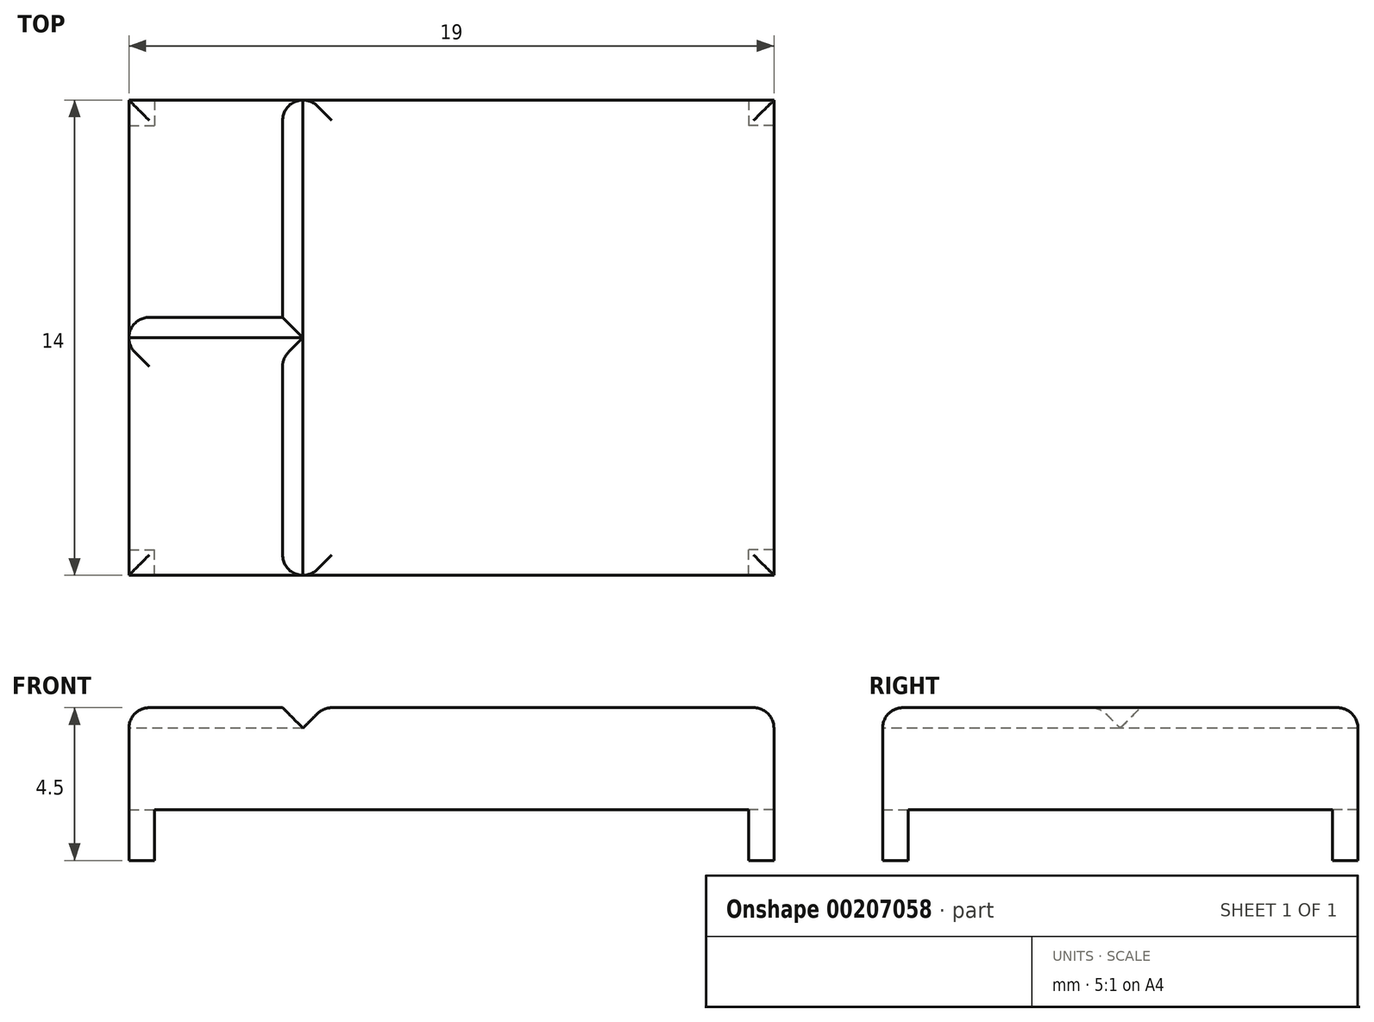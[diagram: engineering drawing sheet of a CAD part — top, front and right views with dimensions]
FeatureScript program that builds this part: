
annotation { "Feature Type Name" : "Feature", "Feature Type Description" : "" }
export const myFeature = defineFeature(function(context is Context, id is Id, definition is map)
    precondition{}
    {
        {
            var Q0;
            Q0=qCreatedBy(makeId("Top.planeOp"),FACE);
            var sketch = newSketch(context, id + "F0", { "sketchPlane" : qUnion([Q0])});
            skLineSegment(sketch, "E0.bottom", {"start": v(9.5, -7) * mm, "end": v(-9.5, -7) * mm});
            skLineSegment(sketch, "E0.top", {"start": v(9.5, 7) * mm, "end": v(-9.5, 7) * mm});
            skLineSegment(sketch, "E0.left", {"start": v(9.5, -7) * mm, "end": v(9.5, 7) * mm});
            skLineSegment(sketch, "E0.right", {"start": v(-9.5, -7) * mm, "end": v(-9.5, 7) * mm});
            skPoint(sketch, "E0.middle", {"position": v(0, 0) * mm});
            skSolve(sketch);
        }
        {
            var Q0;
            Q0=makeQuery(id+"F0.imprint","IMPRINT",FACE,{"disambiguationData":[TD([[makeQuery(id+"F0.imprint","IMPRINT",EDGE,{"derivedFrom":sQuery(id+"F0.wireOp",EDGE,"E0.bottom")}),-1.0]])]});
            extrude(context, id + "F1", {"entities" : qUnion([Q0]), "depth" : 3 * mm});
        }
        {
            var Q0;
            Q0=makeQuery(id+"F1.opExtrude","CAP_FACE",FACE,{"disambiguationData":[OSD([sQuery(id+"F0.wireOp",EDGE,"E0.bottom"),sQuery(id+"F0.wireOp",EDGE,"E0.top"),sQuery(id+"F0.wireOp",EDGE,"E0.left"),sQuery(id+"F0.wireOp",EDGE,"E0.right")])],"isStart":true});
            var sketch = newSketch(context, id + "F2", { "sketchPlane" : qUnion([Q0])});
            skLineSegment(sketch, "E1.bottom", {"start": v(9.5, 7) * mm, "end": v(8.75, 7) * mm});
            skLineSegment(sketch, "E1.top", {"start": v(9.5, 6.25) * mm, "end": v(8.75, 6.25) * mm});
            skLineSegment(sketch, "E1.left", {"start": v(9.5, 7) * mm, "end": v(9.5, 6.25) * mm});
            skLineSegment(sketch, "E1.right", {"start": v(8.75, 7) * mm, "end": v(8.75, 6.25) * mm});
            skLineSegment(sketch, "E2.bottom", {"start": v(-9.5, 7) * mm, "end": v(-8.75, 7) * mm});
            skLineSegment(sketch, "E2.top", {"start": v(-9.5, 6.25) * mm, "end": v(-8.75, 6.25) * mm});
            skLineSegment(sketch, "E2.left", {"start": v(-9.5, 7) * mm, "end": v(-9.5, 6.25) * mm});
            skLineSegment(sketch, "E2.right", {"start": v(-8.75, 7) * mm, "end": v(-8.75, 6.25) * mm});
            skLineSegment(sketch, "E3.bottom", {"start": v(-9.5, -7) * mm, "end": v(-8.75, -7) * mm});
            skLineSegment(sketch, "E3.top", {"start": v(-9.5, -6.25) * mm, "end": v(-8.75, -6.25) * mm});
            skLineSegment(sketch, "E3.left", {"start": v(-9.5, -7) * mm, "end": v(-9.5, -6.25) * mm});
            skLineSegment(sketch, "E3.right", {"start": v(-8.75, -7) * mm, "end": v(-8.75, -6.25) * mm});
            skLineSegment(sketch, "E4.bottom", {"start": v(9.5, -7) * mm, "end": v(8.75, -7) * mm});
            skLineSegment(sketch, "E4.top", {"start": v(9.5, -6.25) * mm, "end": v(8.75, -6.25) * mm});
            skLineSegment(sketch, "E4.left", {"start": v(9.5, -7) * mm, "end": v(9.5, -6.25) * mm});
            skLineSegment(sketch, "E4.right", {"start": v(8.75, -7) * mm, "end": v(8.75, -6.25) * mm});
            skSolve(sketch);
        }
        {
            var Q0;
            Q0=qSketchRegion(id+"F2",true);
            extrude(context, id + "F3", {"entities" : qUnion([Q0]), "operationType" : NewBodyOperationType.ADD, "depth" : 1.5 * mm});
        }
        {
            var Q0;
            Q0=makeQuery(id+"F3.boolean.opBoolean","MERGE",FACE,{"derivedFrom":[makeQuery(id+"F1.opExtrude","SWEPT_FACE",FACE,{"disambiguationData":[OSD([sQuery(id+"F0.wireOp",EDGE,"E0.bottom")])]}),makeQuery(id+"F3.opExtrude","SWEPT_FACE",FACE,{"disambiguationData":[OSD([sQuery(id+"F2.wireOp",EDGE,"E1.bottom")])]}),makeQuery(id+"F3.opExtrude","SWEPT_FACE",FACE,{"disambiguationData":[OSD([sQuery(id+"F2.wireOp",EDGE,"E2.bottom")])]})]});
            var sketch = newSketch(context, id + "F4", { "sketchPlane" : qUnion([Q0])});
            skLineSegment(sketch, "E5", {"start": v(-4.97, 3) * mm, "end": v(-4.37, 2.4) * mm});
            skLineSegment(sketch, "E6", {"start": v(-4.37, 2.4) * mm, "end": v(-3.77, 3) * mm});
            skSolve(sketch);
        }
        {
            var Q0;
            {var subQ0=sQuery(id+"F4.wireOp",EDGE,"E5");Q0=makeQuery(id+"F4.imprint","IMPRINT",FACE,{"disambiguationData":[TD([[makeQuery(id+"F4.imprint","IMPRINT",EDGE,{"derivedFrom":subQ0}),1.0]])]});}
            extrude(context, id + "F5", {"entities" : qUnion([Q0]), "operationType" : NewBodyOperationType.REMOVE, "endBound" : BoundingType.THROUGH_ALL, "oppositeDirection" : true, "depth" : 25 * mm});
        }
        {
            var Q0;
            Q0=makeQuery(id+"F3.boolean.opBoolean","MERGE",FACE,{"derivedFrom":[makeQuery(id+"F1.opExtrude","SWEPT_FACE",FACE,{"disambiguationData":[OSD([sQuery(id+"F0.wireOp",EDGE,"E0.right")])]}),makeQuery(id+"F3.opExtrude","SWEPT_FACE",FACE,{"disambiguationData":[OSD([sQuery(id+"F2.wireOp",EDGE,"E2.left")])]}),makeQuery(id+"F3.opExtrude","SWEPT_FACE",FACE,{"disambiguationData":[OSD([sQuery(id+"F2.wireOp",EDGE,"E3.left")])]})]});
            var sketch = newSketch(context, id + "F6", { "sketchPlane" : qUnion([Q0])});
            skLineSegment(sketch, "E7", {"start": v(-0.6, 3) * mm, "end": v(0, 2.4) * mm});
            skPoint(sketch, "E7.endSnap0", {"position": v(0, 3) * mm});
            skLineSegment(sketch, "E8", {"start": v(0, 2.4) * mm, "end": v(0.6, 3) * mm});
            skSolve(sketch);
        }
        {
            var Q0;
            {var subQ0=sQuery(id+"F6.wireOp",EDGE,"E7");Q0=makeQuery(id+"F6.imprint","IMPRINT",FACE,{"disambiguationData":[TD([[makeQuery(id+"F6.imprint","IMPRINT",EDGE,{"derivedFrom":subQ0}),1.0]])]});}
            extrude(context, id + "F7", {"entities" : qUnion([Q0]), "operationType" : NewBodyOperationType.REMOVE, "endBound" : BoundingType.UP_TO_NEXT, "oppositeDirection" : true, "depth" : 25 * mm});
        }
        {
            var Q0;
            Q0=makeQuery(id+"F5.boolean.opBoolean","COPY",EDGE,{"derivedFrom":makeQuery(id+"F5.opExtrude","SWEPT_EDGE",EDGE,{"disambiguationData":[OSD([sQuery(id+"F0.wireOp",EDGE,"E0.bottom"),sQuery(id+"F4.wireOp",EDGE,"E6")])]})});
            var Q1;
            {var subQ0=sQuery(id+"F0.wireOp",EDGE,"E0.top");var subQ1=sQuery(id+"F0.wireOp",EDGE,"E0.bottom");var subQ2=sQuery(id+"F4.wireOp",EDGE,"E5");Q1=makeQuery(id+"F7.boolean.opBoolean","SPLIT",EDGE,{"disambiguationData":[TD([makeQuery(id+"F1.opExtrude","SWEPT_FACE",FACE,{"disambiguationData":[OSD([subQ0])]})])],"derivedFrom":makeQuery(id+"F5.boolean.opBoolean","COPY",EDGE,{"derivedFrom":makeQuery(id+"F5.opExtrude","SWEPT_EDGE",EDGE,{"disambiguationData":[OSD([subQ1,subQ2])]})})});}
            var Q2;
            {var subQ0=sQuery(id+"F0.wireOp",EDGE,"E0.bottom");var subQ1=sQuery(id+"F4.wireOp",EDGE,"E5");Q2=makeQuery(id+"F7.boolean.opBoolean","SPLIT",EDGE,{"disambiguationData":[TD([makeQuery(id+"F1.opExtrude","SWEPT_FACE",FACE,{"disambiguationData":[OSD([subQ0])]})])],"derivedFrom":makeQuery(id+"F5.boolean.opBoolean","COPY",EDGE,{"derivedFrom":makeQuery(id+"F5.opExtrude","SWEPT_EDGE",EDGE,{"disambiguationData":[OSD([subQ0,subQ1])]})})});}
            var Q3;
            Q3=makeQuery(id+"F7.boolean.opBoolean","COPY",EDGE,{"derivedFrom":makeQuery(id+"F7.opExtrude","SWEPT_EDGE",EDGE,{"disambiguationData":[OSD([sQuery(id+"F0.wireOp",EDGE,"E0.right"),sQuery(id+"F6.wireOp",EDGE,"E8")])]})});
            var Q4;
            Q4=makeQuery(id+"F7.boolean.opBoolean","COPY",EDGE,{"derivedFrom":makeQuery(id+"F7.opExtrude","SWEPT_EDGE",EDGE,{"disambiguationData":[OSD([sQuery(id+"F0.wireOp",EDGE,"E0.right"),sQuery(id+"F6.wireOp",EDGE,"E7")])]})});
            var Q5;
            {var subQ0=sQuery(id+"F0.wireOp",EDGE,"E0.left");var subQ1=sQuery(id+"F0.wireOp",EDGE,"E0.bottom");Q5=makeQuery(id+"F5.boolean.opBoolean","SPLIT",EDGE,{"disambiguationData":[TD([makeQuery(id+"F1.opExtrude","SWEPT_FACE",FACE,{"disambiguationData":[OSD([subQ0])]})])],"derivedFrom":makeQuery(id+"F1.opExtrude","CAP_EDGE",EDGE,{"disambiguationData":[OSD([subQ1])],"isStart":false})});}
            var Q6;
            {var subQ0=sQuery(id+"F0.wireOp",EDGE,"E0.right");var subQ1=sQuery(id+"F0.wireOp",EDGE,"E0.bottom");Q6=makeQuery(id+"F5.boolean.opBoolean","SPLIT",EDGE,{"disambiguationData":[TD([makeQuery(id+"F1.opExtrude","SWEPT_FACE",FACE,{"disambiguationData":[OSD([subQ0])]})])],"derivedFrom":makeQuery(id+"F1.opExtrude","CAP_EDGE",EDGE,{"disambiguationData":[OSD([subQ1])],"isStart":false})});}
            var Q7;
            {var subQ0=sQuery(id+"F0.wireOp",EDGE,"E0.left");var subQ1=sQuery(id+"F0.wireOp",EDGE,"E0.top");Q7=makeQuery(id+"F5.boolean.opBoolean","SPLIT",EDGE,{"disambiguationData":[TD([makeQuery(id+"F1.opExtrude","SWEPT_FACE",FACE,{"disambiguationData":[OSD([subQ0])]})])],"derivedFrom":makeQuery(id+"F1.opExtrude","CAP_EDGE",EDGE,{"disambiguationData":[OSD([subQ1])],"isStart":false})});}
            var Q8;
            Q8=makeQuery(id+"F1.opExtrude","CAP_EDGE",EDGE,{"disambiguationData":[OSD([sQuery(id+"F0.wireOp",EDGE,"E0.left")])],"isStart":false});
            var Q9;
            {var subQ0=sQuery(id+"F0.wireOp",EDGE,"E0.right");var subQ1=sQuery(id+"F0.wireOp",EDGE,"E0.top");Q9=makeQuery(id+"F5.boolean.opBoolean","SPLIT",EDGE,{"disambiguationData":[TD([makeQuery(id+"F1.opExtrude","SWEPT_FACE",FACE,{"disambiguationData":[OSD([subQ0])]})])],"derivedFrom":makeQuery(id+"F1.opExtrude","CAP_EDGE",EDGE,{"disambiguationData":[OSD([subQ1])],"isStart":false})});}
            var Q10;
            {var subQ0=sQuery(id+"F0.wireOp",EDGE,"E0.right");var subQ1=sQuery(id+"F0.wireOp",EDGE,"E0.top");Q10=makeQuery(id+"F7.boolean.opBoolean","SPLIT",EDGE,{"disambiguationData":[TD([makeQuery(id+"F1.opExtrude","SWEPT_FACE",FACE,{"disambiguationData":[OSD([subQ1])]})])],"derivedFrom":makeQuery(id+"F1.opExtrude","CAP_EDGE",EDGE,{"disambiguationData":[OSD([subQ0])],"isStart":false})});}
            var Q11;
            {var subQ0=sQuery(id+"F0.wireOp",EDGE,"E0.right");var subQ1=sQuery(id+"F0.wireOp",EDGE,"E0.bottom");Q11=makeQuery(id+"F7.boolean.opBoolean","SPLIT",EDGE,{"disambiguationData":[TD([makeQuery(id+"F1.opExtrude","SWEPT_FACE",FACE,{"disambiguationData":[OSD([subQ1])]})])],"derivedFrom":makeQuery(id+"F1.opExtrude","CAP_EDGE",EDGE,{"disambiguationData":[OSD([subQ0])],"isStart":false})});}
            fillet(context, id + "F8", {"entities" : qUnion([Q0, Q1, Q2, Q3, Q4, Q5, Q6, Q7, Q8, Q9, Q10, Q11]), "radius" : 0.6 * mm, "tangentPropagation" : true, "allowEdgeOverflow" : false});
        }
    });
